FCSTD DOCUMENT  (FreeCAD 0.18R16146 (Git))
Label: icons
License: All rights reserved
LicenseURL: http://en.wikipedia.org/wiki/All_rights_reserved
objects: Sketcher::SketchObject×4, Spreadsheet::Sheet×1
note: 4 computed .brp shape members not serialized (recipe doc carries the construction recipe); baked Part::Feature solids carry a one-line shape summary decoded from their .brp

FEATURE [Sketcher::SketchObject] Sketch  label="fail"
  expr: Constraints[35] = ss.radius
  expr: Constraints[37] = ss.radius
  expr: Constraints[38] = ss.radius
  expr: Constraints[39] = ss.radius
  expr: Constraints[40] = ss.radius
  expr: Constraints[41] = ss.radius
  expr: Constraints[42] = ss.radius
  expr: Constraints[36] = ss.radius
  expr: Constraints[67] = ss.mainr
  expr: Constraints[59] = ss.fillet
  sketch-geometry (27):
    g0: Circle [constr] CenterX=0 CenterY=0 CenterZ=0 NormalX=0 NormalY=0 NormalZ=1 AngleXU=0 Radius=50
    g1: GeomPoint X=0 Y=0 Z=0
    g2: GeomPoint X=0 Y=0 Z=0
    g3: LineSegment [constr] StartX=0 StartY=0 StartZ=0 EndX=35.3553 EndY=35.3553 EndZ=0
    g4: LineSegment [constr] StartX=0 StartY=0 StartZ=0 EndX=35.3553 EndY=-35.3553 EndZ=0
    g5: LineSegment [constr] StartX=0 StartY=0 StartZ=0 EndX=-35.3553 EndY=-35.3553 EndZ=0
    g6: LineSegment [constr] StartX=0 StartY=0 StartZ=0 EndX=-35.3553 EndY=35.3553 EndZ=0
    g7: LineSegment StartX=29.6985 StartY=36.7696 StartZ=0 EndX=3.6e-15 EndY=7.07107 EndZ=0
    g8: LineSegment StartX=36.7696 StartY=29.6985 StartZ=0 EndX=7.07107 EndY=0 EndZ=0
    g9: LineSegment StartX=36.7696 StartY=33.9411 StartZ=0 EndX=33.9411 EndY=36.7696 EndZ=0
    g10: LineSegment StartX=7.07107 StartY=0 StartZ=0 EndX=36.7696 EndY=-29.6985 EndZ=0
    g11: LineSegment StartX=36.7696 StartY=-33.9411 StartZ=0 EndX=33.9411 EndY=-36.7696 EndZ=0
    g12: LineSegment StartX=29.6985 StartY=-36.7696 StartZ=0 EndX=-3.6e-15 EndY=-7.07107 EndZ=0
    g13: LineSegment StartX=-3.6e-15 StartY=-7.07107 StartZ=0 EndX=-29.6985 EndY=-36.7696 EndZ=0
    g14: LineSegment StartX=-33.9411 StartY=-36.7696 StartZ=0 EndX=-36.7696 EndY=-33.9411 EndZ=0
    g15: LineSegment StartX=-36.7696 StartY=-29.6985 StartZ=0 EndX=-7.07107 EndY=-3.6e-15 EndZ=0
    g16: LineSegment StartX=-7.07107 StartY=9e-16 StartZ=0 EndX=-36.7696 EndY=29.6985 EndZ=0
    g17: LineSegment StartX=-36.7696 StartY=33.9411 StartZ=0 EndX=-33.9411 EndY=36.7696 EndZ=0
    g18: LineSegment StartX=-29.6985 StartY=36.7696 StartZ=0 EndX=3.6e-15 EndY=7.07107 EndZ=0
    g19: ArcOfCircle CenterX=34.6482 CenterY=31.8198 CenterZ=0 NormalX=0 NormalY=0 NormalZ=1 AngleXU=0 Radius=3 StartAngle=5.49779 EndAngle=7.06858
    g20: ArcOfCircle CenterX=31.8198 CenterY=34.6482 CenterZ=0 NormalX=0 NormalY=0 NormalZ=1 AngleXU=0 Radius=3 StartAngle=0.785398 EndAngle=2.35619
    g21: ArcOfCircle CenterX=-31.8198 CenterY=34.6482 CenterZ=0 NormalX=0 NormalY=0 NormalZ=1 AngleXU=0 Radius=3 StartAngle=0.785398 EndAngle=2.35619
    g22: ArcOfCircle CenterX=-34.6482 CenterY=31.8198 CenterZ=0 NormalX=0 NormalY=0 NormalZ=1 AngleXU=0 Radius=3 StartAngle=2.35619 EndAngle=3.92699
    g23: ArcOfCircle CenterX=-34.6482 CenterY=-31.8198 CenterZ=0 NormalX=0 NormalY=0 NormalZ=1 AngleXU=0 Radius=3 StartAngle=2.35619 EndAngle=3.92699
    g24: ArcOfCircle CenterX=-31.8198 CenterY=-34.6482 CenterZ=0 NormalX=0 NormalY=0 NormalZ=1 AngleXU=0 Radius=3 StartAngle=3.92699 EndAngle=5.49779
    g25: ArcOfCircle CenterX=31.8198 CenterY=-34.6482 CenterZ=0 NormalX=0 NormalY=0 NormalZ=1 AngleXU=0 Radius=3 StartAngle=3.92699 EndAngle=5.49779
    g26: ArcOfCircle CenterX=34.6482 CenterY=-31.8198 CenterZ=0 NormalX=0 NormalY=0 NormalZ=1 AngleXU=0 Radius=3 StartAngle=5.49779 EndAngle=7.06858
  constraints (62):
    c: Coincident(g1,g0)
    c: Coincident(g1,g2)
    c: Coincident(g-1,g1)
    c: PointOnObject(g3,g0)
    c: Coincident(g3,g1)
    c: Coincident(g4,g1)
    c: PointOnObject(g4,g0)
    c: Coincident(g5,g1)
    c: PointOnObject(g5,g0)
    c: Coincident(g6,g1)
    c: PointOnObject(g6,g0)
    c: Parallel(g4,g6)
    c: Parallel(g3,g5)
    c: Angle(g-1,g3) = 0.785398
    c: Angle(g3,g6) = 1.5708
    c: Parallel(g3,g7)
    c: Parallel(g3,g8)
    c: PointOnObject(g3,g9)
    c: Coincident(g10,g8)
    c: Coincident(g13,g12)
    c: Coincident(g16,g15)
    c: Coincident(g18,g7)
    c: Parallel(g18,g6)
    c: Parallel(g6,g16)
    c: Parallel(g10,g4)
    c: Parallel(g12,g4)
    c: Parallel(g13,g5)
    c: Parallel(g15,g5)
    c: Perpendicular(g3,g9)
    c: Perpendicular(g11,g4)
    c: Perpendicular(g14,g5)
    c: Perpendicular(g17,g6)
    c: PointOnObject(g6,g17)
    c: PointOnObject(g5,g14)
    c: PointOnObject(g4,g11)
    c: Distance(g8,g4) = 5
    c: Distance(g8,g3) = 5
    c: Distance(g12,g4) = 5
    c: Distance(g12,g5) = 5
    c: Distance(g15,g5) = 5
    c: Distance(g15,g6) = 5
    c: Distance(g7,g6) = 5
    c: Distance(g7,g3) = 5
    c: Tangent(g8,g19) = 1.5708
    c: Tangent(g9,g19) = -1.5708
    c: Tangent(g7,g20) = -1.5708
    c: Tangent(g9,g20) = -1.5708
    c: Tangent(g17,g21) = 1.5708
    c: Tangent(g18,g21) = 1.5708
    c: Tangent(g16,g22) = 1.5708
    c: Tangent(g17,g22) = 1.5708
    c: Tangent(g14,g23) = 1.5708
    c: Tangent(g15,g23) = 1.5708
    c: Tangent(g13,g24) = 1.5708
    c: Tangent(g14,g24) = 1.5708
    c: Tangent(g11,g25) = 1.5708
    c: Tangent(g12,g25) = 1.5708
    c: Tangent(g10,g26) = 1.5708
    c: Tangent(g11,g26) = 1.5708
    c: Radius(g19) = 3
    c: Equal(g19, g20-g26) x7
    c: Radius(g0) = 50
FEATURE [Spreadsheet::Sheet] Spreadsheet  label="ss"
  cells = A1=main radius; B1(mainr)==50mm; A2=emboss radius; B2(radius)==5mm; A3=fillet; B3(fillet)==3mm; A4=bounds; B4(bounds)==120mm; A7=initial icon width; B7(mwidth)==60mm
FEATURE [Sketcher::SketchObject] Sketch001  label="success"
  expr: Constraints[48] = ss.mainr
  expr: Constraints[16] = ss.radius
  expr: Constraints[15] = ss.radius
  expr: Constraints[13] = ss.radius
  expr: Constraints[14] = ss.radius
  sketch-geometry (20):
    g0: LineSegment [constr] StartX=-18.1802 StartY=-32.3223 StartZ=0 EndX=50 EndY=35.8579 EndZ=0
    g1: LineSegment [constr] StartX=-18.1802 StartY=-32.3223 StartZ=0 EndX=-50 EndY=-0.502525 EndZ=0
    g2: LineSegment StartX=-18.1802 StartY=-25.2513 StartZ=0 EndX=43.636 EndY=36.565 EndZ=0
    g3: LineSegment StartX=49.2929 StartY=36.565 StartZ=0 EndX=50.7071 EndY=35.1508 EndZ=0
    g4: LineSegment StartX=50.7071 StartY=29.4939 StartZ=0 EndX=-18.1802 EndY=-39.3934 EndZ=0
    g5: LineSegment StartX=-18.1802 StartY=-39.3934 StartZ=0 EndX=-50.7071 EndY=-6.86649 EndZ=0
    g6: LineSegment StartX=-50.7071 StartY=-1.20963 StartZ=0 EndX=-49.2929 EndY=0.204581 EndZ=0
    g7: LineSegment StartX=-43.636 StartY=0.204581 StartZ=0 EndX=-18.1802 EndY=-25.2513 EndZ=0
    g8: ArcOfCircle CenterX=46.4645 CenterY=33.7365 CenterZ=0 NormalX=0 NormalY=0 NormalZ=1 AngleXU=0 Radius=4 StartAngle=0.785398 EndAngle=2.35619
    g9: ArcOfCircle CenterX=47.8787 CenterY=32.3223 CenterZ=0 NormalX=0 NormalY=0 NormalZ=1 AngleXU=0 Radius=4 StartAngle=5.49779 EndAngle=7.06858
    g10: ArcOfCircle CenterX=-46.4645 CenterY=-2.62385 CenterZ=0 NormalX=0 NormalY=0 NormalZ=1 AngleXU=0 Radius=4 StartAngle=0.785398 EndAngle=2.35619
    g11: ArcOfCircle CenterX=-47.8787 CenterY=-4.03806 CenterZ=0 NormalX=0 NormalY=0 NormalZ=1 AngleXU=0 Radius=4 StartAngle=2.35619 EndAngle=3.92699
    g12: GeomPoint X=0 Y=0 Z=0
    g13: GeomPoint X=0 Y=0 Z=0
    g14: LineSegment [constr] StartX=-50 StartY=-50 StartZ=0 EndX=50 EndY=-50 EndZ=0
    g15: LineSegment [constr] StartX=50 StartY=-50 StartZ=0 EndX=50 EndY=50 EndZ=0
    g16: LineSegment [constr] StartX=50 StartY=50 StartZ=0 EndX=-50 EndY=50 EndZ=0
    g17: LineSegment [constr] StartX=-50 StartY=50 StartZ=0 EndX=-50 EndY=-50 EndZ=0
    g18: LineSegment [constr] StartX=-18.1802 StartY=-32.3223 StartZ=0 EndX=-21.7157 EndY=-35.8579 EndZ=0
    g19: GeomPoint X=14.1421 Y=0 Z=0
  constraints (49):
    c: Coincident(g1,g0)
    c: Angle(g0,g1) = 1.5708
    c: Angle(g-1,g0) = 0.785398
    c: Coincident(g5,g4)
    c: Coincident(g7,g2)
    c: PointOnObject(g0,g3)
    c: PointOnObject(g1,g6)
    c: Parallel(g7,g1)
    c: Parallel(g5,g1)
    c: Parallel(g4,g0)
    c: Parallel(g2,g0)
    c: Perpendicular(g0,g3)
    c: Perpendicular(g1,g6)
    c: Distance(g2,g0) = 5
    c: Distance(g2,g1) = 5
    c: Distance(g4,g0) = 5
    c: Distance(g4,g1) = 5
    c: Tangent(g2,g8) = 1.5708
    c: Tangent(g3,g8) = 1.5708
    c: Tangent(g3,g9) = 1.5708
    c: Tangent(g4,g9) = 1.5708
    c: Tangent(g6,g10) = 1.5708
    c: Tangent(g7,g10) = 1.5708
    c: Tangent(g5,g11) = 1.5708
    c: Tangent(g6,g11) = 1.5708
    c: Radius(g8) = 4
    c: Equal(g8,g9)
    c: Equal(g8,g10)
    c: Equal(g8,g11)
    c: Coincident(g12,g13)
    c: Coincident(g-1,g12)
    c: Coincident(g14,g15)
    c: Coincident(g15,g16)
    c: Coincident(g16,g17)
    c: Coincident(g17,g14)
    c: Horizontal(g14)
    c: Vertical(g15)
    c: Equal(g16,g17)
    c: PointOnObject(g1,g17)
    c: PointOnObject(g0,g15)
    c: Coincident(g18,g0)
    c: PointOnObject(g18,g5)
    c: Perpendicular(g5,g18)
    c: Distance(g12,g0) = 10
    c: Symmetric(g0,g18,g19)
    c: PointOnObject(g19,g-1)
    c: Symmetric(g16,g14,g-1)
    c: Symmetric(g16,g15,g-2)
    c: Distance(g12,g15) = 50
FEATURE [Sketcher::SketchObject] Sketch002  label="initial"
  expr: Constraints[18] = ss.fillet
  expr: Constraints[22] = ss.mwidth
  expr: Constraints[9] = ss.radius
  expr: Constraints[8] = ss.radius
  sketch-geometry (9):
    g0: LineSegment StartX=-27 StartY=5 StartZ=0 EndX=27 EndY=5 EndZ=0
    g1: LineSegment StartX=30 StartY=2 StartZ=0 EndX=30 EndY=-2 EndZ=0
    g2: LineSegment StartX=27 StartY=-5 StartZ=0 EndX=-27 EndY=-5 EndZ=0
    g3: LineSegment StartX=-30 StartY=-2 StartZ=0 EndX=-30 EndY=2 EndZ=0
    g4: LineSegment [constr] StartX=-30 StartY=0 StartZ=0 EndX=30 EndY=0 EndZ=0
    g5: ArcOfCircle CenterX=-27 CenterY=2 CenterZ=0 NormalX=0 NormalY=0 NormalZ=1 AngleXU=0 Radius=3 StartAngle=1.5708 EndAngle=3.14159
    g6: ArcOfCircle CenterX=27 CenterY=2 CenterZ=0 NormalX=0 NormalY=0 NormalZ=1 AngleXU=0 Radius=3 StartAngle=1e-16 EndAngle=1.5708
    g7: ArcOfCircle CenterX=27 CenterY=-2 CenterZ=0 NormalX=0 NormalY=0 NormalZ=1 AngleXU=0 Radius=3 StartAngle=4.71239 EndAngle=6.28319
    g8: ArcOfCircle CenterX=-27 CenterY=-2 CenterZ=0 NormalX=0 NormalY=0 NormalZ=1 AngleXU=0 Radius=3 StartAngle=3.14159 EndAngle=4.71239
  constraints (23):
    c: Horizontal(g0)
    c: Horizontal(g2)
    c: Vertical(g3)
    c: Vertical(g1)
    c: Horizontal(g4)
    c: Symmetric(g4,g4,g-1)
    c: PointOnObject(g4,g1)
    c: PointOnObject(g4,g3)
    c: Distance(g-1,g0) = 5
    c: Distance(g-1,g2) = 5
    c: Tangent(g0,g5) = 1.5708
    c: Tangent(g3,g5) = 1.5708
    c: Tangent(g0,g6) = 1.5708
    c: Tangent(g1,g6) = 1.5708
    c: Tangent(g1,g7) = 1.5708
    c: Tangent(g2,g7) = 1.5708
    c: Tangent(g2,g8) = 1.5708
    c: Tangent(g3,g8) = 1.5708
    c: Radius(g5) = 3
    c: Equal(g5,g6)
    c: Equal(g5,g7)
    c: Equal(g5,g8)
    c: Distance(g4,g4) = 60
FEATURE [Sketcher::SketchObject] Sketch003  label="bounds"
  expr: Constraints[9] = ss.bounds
  sketch-geometry (4):
    g0: LineSegment StartX=-60 StartY=-60 StartZ=0 EndX=60 EndY=-60 EndZ=0
    g1: LineSegment StartX=60 StartY=-60 StartZ=0 EndX=60 EndY=60 EndZ=0
    g2: LineSegment StartX=60 StartY=60 StartZ=0 EndX=-60 EndY=60 EndZ=0
    g3: LineSegment StartX=-60 StartY=60 StartZ=0 EndX=-60 EndY=-60 EndZ=0
  constraints (10):
    c: Coincident(g0,g1)
    c: Coincident(g1,g2)
    c: Coincident(g2,g3)
    c: Coincident(g3,g0)
    c: Horizontal(g0)
    c: Vertical(g1)
    c: Equal(g2,g3)
    c: Symmetric(g2,g0,g-1)
    c: Symmetric(g2,g1,g-2)
    c: Distance(g2) = 120
